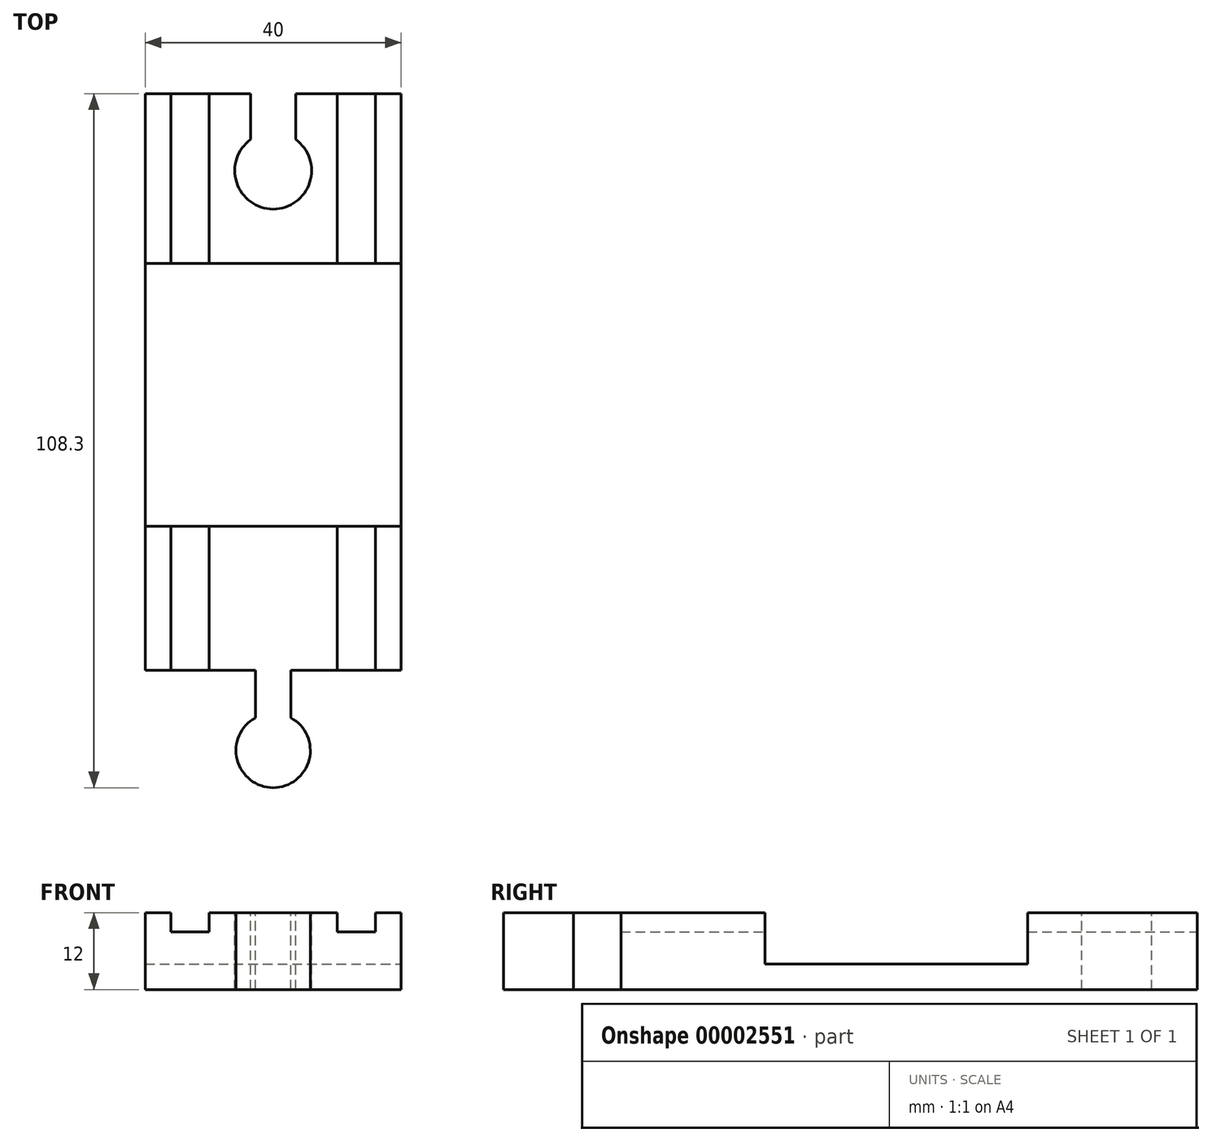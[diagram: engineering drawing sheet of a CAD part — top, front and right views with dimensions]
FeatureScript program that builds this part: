
annotation { "Feature Type Name" : "Feature", "Feature Type Description" : "" }
export const myFeature = defineFeature(function(context is Context, id is Id, definition is map)
    precondition{}
    {
        {
            var Q0;
            Q0=qCreatedBy(makeId("Front.planeOp"),FACE);
            var sketch = newSketch(context, id + "F0", { "sketchPlane" : qUnion([Q0])});
            skLineSegment(sketch, "E0.bottom", {"start": v(0, 0) * mm, "end": v(40, 0) * mm});
            skLineSegment(sketch, "E0.top", {"start": v(0, 12) * mm, "end": v(40, 12) * mm});
            skLineSegment(sketch, "E0.left", {"start": v(0, 0) * mm, "end": v(0, 12) * mm});
            skLineSegment(sketch, "E0.right", {"start": v(40, 0) * mm, "end": v(40, 12) * mm});
            skLineSegment(sketch, "E1.bottom", {"start": v(36, 12) * mm, "end": v(30, 12) * mm});
            skLineSegment(sketch, "E1.top", {"start": v(36, 9) * mm, "end": v(30, 9) * mm});
            skLineSegment(sketch, "E1.left", {"start": v(36, 12) * mm, "end": v(36, 9) * mm});
            skLineSegment(sketch, "E1.right", {"start": v(30, 12) * mm, "end": v(30, 9) * mm});
            skLineSegment(sketch, "E2", {"start": v(20, 12) * mm, "end": v(20, 0) * mm, "construction": true});
            skLineSegment(sketch, "E3.0.MirrorCS", {"start": v(10, 12) * mm, "end": v(10, 9) * mm});
            skLineSegment(sketch, "E3.1.MirrorCS", {"start": v(4, 9) * mm, "end": v(10, 9) * mm});
            skLineSegment(sketch, "E3.2.MirrorCS", {"start": v(4, 12) * mm, "end": v(4, 9) * mm});
            skSolve(sketch);
        }
        {
            var Q0;
            Q0=makeQuery(id+"F0.imprint","IMPRINT",FACE,{"disambiguationData":[TD([[makeQuery(id+"F0.imprint","IMPRINT",EDGE,{"derivedFrom":sQuery(id+"F0.wireOp",EDGE,"E0.bottom")}),1.0]])]});
            extrude(context, id + "F1", {"entities" : qUnion([Q0]), "depth" : 90 * mm});
        }
        {
            var Q0;
            {var subQ0=sQuery(id+"F0.wireOp",EDGE,"E0.top");Q0=makeQuery(id+"F1.opExtrude","SWEPT_FACE",FACE,{"disambiguationData":[OSD([subQ0]),TDD([makeQuery(id+"F0.imprint","IMPRINT",EDGE,{"disambiguationData":[TD([[makeQuery(id+"F0.imprint","INTERSECT",VERTEX,{"derivedFrom":[subQ0,sQuery(id+"F0.wireOp",EDGE,"E3.0.MirrorCS")]}),-1.0]])],"derivedFrom":subQ0})])]});}
            var sketch = newSketch(context, id + "F2", { "sketchPlane" : qUnion([Q0])});
            skLineSegment(sketch, "E4", {"start": v(20, 0) * mm, "end": v(20, -90) * mm, "construction": true});
            skArc(sketch, "E5", {"start": v(16.5, -7.13) * mm, "mid": v(20, -18) * mm, "end": v(23.5, -7.13) * mm});
            skLineSegment(sketch, "E6.rect.bottom", {"start": v(23.5, 0) * mm, "end": v(16.5, 0) * mm});
            skLineSegment(sketch, "E6.rect.left", {"start": v(23.5, 0) * mm, "end": v(23.5, -7.13) * mm});
            skLineSegment(sketch, "E6.rect.right", {"start": v(16.5, 0) * mm, "end": v(16.5, -7.13) * mm});
            skPoint(sketch, "E6.rect.middle", {"position": v(20, -6) * mm});
            skSolve(sketch);
        }
        {
            var Q0;
            Q0=makeQuery(id+"F2.imprint","IMPRINT",FACE,{"disambiguationData":[TD([[makeQuery(id+"F2.imprint","IMPRINT",EDGE,{"derivedFrom":sQuery(id+"F2.wireOp",EDGE,"E5")}),1.0]])]});
            extrude(context, id + "F3", {"entities" : qUnion([Q0]), "operationType" : NewBodyOperationType.REMOVE, "endBound" : BoundingType.UP_TO_NEXT, "oppositeDirection" : true, "depth" : 25 * mm});
        }
        {
            var Q0;
            {var subQ0=sQuery(id+"F0.wireOp",EDGE,"E0.top");Q0=makeQuery(id+"F1.opExtrude","SWEPT_FACE",FACE,{"disambiguationData":[OSD([subQ0]),TDD([makeQuery(id+"F0.imprint","IMPRINT",EDGE,{"disambiguationData":[TD([[makeQuery(id+"F0.imprint","INTERSECT",VERTEX,{"derivedFrom":[subQ0,sQuery(id+"F0.wireOp",EDGE,"E3.0.MirrorCS")]}),-1.0]])],"derivedFrom":subQ0})])]});}
            var sketch = newSketch(context, id + "F4", { "sketchPlane" : qUnion([Q0])});
            skLineSegment(sketch, "E7.rect.bottom", {"start": v(22.75, -102.5) * mm, "end": v(17.25, -102.5) * mm});
            skLineSegment(sketch, "E7.rect.top", {"start": v(22.75, -77.5) * mm, "end": v(17.25, -77.5) * mm});
            skLineSegment(sketch, "E7.rect.left", {"start": v(22.75, -102.5) * mm, "end": v(22.75, -77.5) * mm});
            skLineSegment(sketch, "E7.rect.right", {"start": v(17.25, -102.5) * mm, "end": v(17.25, -77.5) * mm});
            skPoint(sketch, "E7.rect.middle", {"position": v(20, -90) * mm});
            skCircle(sketch, "E8", {"center": v(20, -102.5) * mm, "radius": 5.8 * mm});
            skSolve(sketch);
        }
        {
            var Q0;
            {var subQ4=sQuery(id+"F4.wireOp",EDGE,"E7.rect.left");var subQ6=sQuery(id+"F4.wireOp",EDGE,"E8");var subQ8=makeQuery(id+"F4.imprint","INTERSECT",VERTEX,{"derivedFrom":[subQ4,subQ6]});Q0=makeQuery(id+"F4.imprint","IMPRINT",FACE,{"disambiguationData":[TD([[makeQuery(id+"F4.imprint","IMPRINT",EDGE,{"disambiguationData":[TD([[subQ8,-1.0]])],"derivedFrom":subQ6}),-1.0]])]});}
            var Q1;
            {var subQ5=sQuery(id+"F4.wireOp",EDGE,"E7.rect.bottom");Q1=makeQuery(id+"F4.imprint","IMPRINT",FACE,{"disambiguationData":[TD([[makeQuery(id+"F4.imprint","IMPRINT",EDGE,{"derivedFrom":subQ5}),1.0]])]});}
            var Q2;
            {var subQ5=sQuery(id+"F4.wireOp",EDGE,"E7.rect.bottom");Q2=makeQuery(id+"F4.imprint","IMPRINT",FACE,{"disambiguationData":[TD([[makeQuery(id+"F4.imprint","IMPRINT",EDGE,{"derivedFrom":subQ5}),-1.0]])]});}
            var Q3;
            Q3=makeQuery(id+"F1.opExtrude","SWEPT_FACE",FACE,{"disambiguationData":[OSD([sQuery(id+"F0.wireOp",EDGE,"E0.bottom")])]});
            extrude(context, id + "F5", {"entities" : qUnion([Q0, Q1, Q2]), "operationType" : NewBodyOperationType.ADD, "endBound" : BoundingType.UP_TO_SURFACE, "oppositeDirection" : true, "endBoundEntityFace" : qUnion([Q3]), "depth" : 25 * mm});
        }
        {
            var Q0;
            {var subQ0=sQuery(id+"F0.wireOp",EDGE,"E0.top");Q0=makeQuery(id+"F5.boolean.opBoolean","MERGE",FACE,{"derivedFrom":[makeQuery(id+"F1.opExtrude","SWEPT_FACE",FACE,{"disambiguationData":[OSD([subQ0]),TDD([makeQuery(id+"F0.imprint","IMPRINT",EDGE,{"disambiguationData":[TD([[makeQuery(id+"F0.imprint","INTERSECT",VERTEX,{"derivedFrom":[subQ0,sQuery(id+"F0.wireOp",EDGE,"E3.0.MirrorCS")]}),-1.0]])],"derivedFrom":subQ0})])]}),makeQuery(id+"F5.opExtrude","CAP_FACE",FACE,{"disambiguationData":[OSD([subQ0,sQuery(id+"F4.wireOp",EDGE,"E7.rect.left"),sQuery(id+"F4.wireOp",EDGE,"E7.rect.right"),sQuery(id+"F4.wireOp",EDGE,"E8")])],"isStart":true})]});}
            var sketch = newSketch(context, id + "F6", { "sketchPlane" : qUnion([Q0])});
            skLineSegment(sketch, "E9.bottom", {"start": v(0, -67.5) * mm, "end": v(40, -67.5) * mm});
            skLineSegment(sketch, "E9.top", {"start": v(0, -26.5) * mm, "end": v(40, -26.5) * mm});
            skLineSegment(sketch, "E9.left", {"start": v(0, -67.5) * mm, "end": v(0, -26.5) * mm});
            skLineSegment(sketch, "E9.right", {"start": v(40, -67.5) * mm, "end": v(40, -26.5) * mm});
            skSolve(sketch);
        }
        {
            var Q0;
            {var subQ0=sQuery(id+"F0.wireOp",EDGE,"E0.top");var subQ1=makeQuery(id+"F1.opExtrude","SWEPT_EDGE",EDGE,{"disambiguationData":[OSD([subQ0,sQuery(id+"F0.wireOp",EDGE,"E3.0.MirrorCS")])]});var subQ4=sQuery(id+"F6.wireOp",EDGE,"E9.bottom");var subQ5=makeQuery(id+"F6.imprint","INTERSECT",VERTEX,{"derivedFrom":[subQ1,subQ4]});var subQ7=sQuery(id+"F6.wireOp",EDGE,"E9.left");var subQ12=sQuery(id+"F6.wireOp",EDGE,"E9.right");Q0=qUnion([makeQuery(id+"F6.imprint","IMPRINT",FACE,{"disambiguationData":[TD([[makeQuery(id+"F6.imprint","IMPRINT",EDGE,{"derivedFrom":subQ7}),-1.0]])]}),makeQuery(id+"F6.imprint","IMPRINT",FACE,{"disambiguationData":[TD([[makeQuery(id+"F6.imprint","IMPRINT",EDGE,{"derivedFrom":subQ12}),1.0]])]}),makeQuery(id+"F6.imprint","IMPRINT",FACE,{"disambiguationData":[TD([[makeQuery(id+"F6.imprint","IMPRINT",EDGE,{"disambiguationData":[TD([[subQ5,-1.0]])],"derivedFrom":subQ4}),1.0]])]})]);}
            extrude(context, id + "F7", {"entities" : qUnion([Q0]), "operationType" : NewBodyOperationType.REMOVE, "oppositeDirection" : true, "depth" : 8 * mm});
        }
    });
